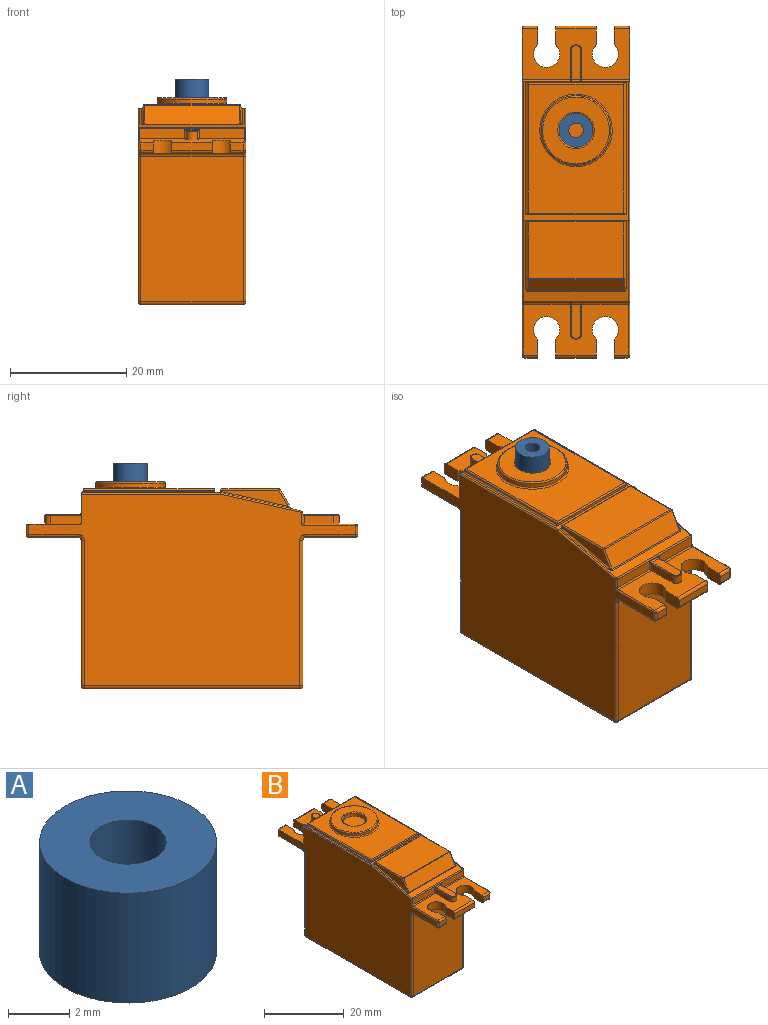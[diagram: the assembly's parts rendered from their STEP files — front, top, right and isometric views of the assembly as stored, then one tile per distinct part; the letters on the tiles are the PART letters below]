
ASSEMBLY  parts=2 mates=1
PART A: 4 faces, bbox 5.8x5.8x4.4 mm
  f0: cylinder r=2.9mm len=5.8mm, axis (0,0,-1), area 80.2mm2, adj f1,f2
  f1: plane 5.8x5.8mm, normal (0,0,1), area 21.5mm2, adj f0,f3
  f2: plane 5.8x5.8mm, normal (0,0,-1), area 21.5mm2, adj f0,f3
  f3: cylinder r=1.25mm len=4.4mm, axis (0,0,1), area 34.6mm2, adj f1,f2
PART B: 154 faces, bbox 18.6x57.2x35.7 mm
  f0: plane 18.1x8.75mm, normal (0,0,1), area 100.9mm2, adj f9,f10,f41,f42,f43,f82,f84,f88
  f1: plane 7x1.3mm, normal (0,-1,0), area 9.1mm2, adj f7,f9,f149,f151
  f2: plane 2.2x1.3mm, normal (0,-1,0), area 2.9mm2, adj f8,f10,f128,f150
  f3: plane 17.6x8.5mm, normal (0,0,-1), area 103.4mm2, adj f13,f14,f106,f108,f109,f140,f142,f143
  f4: plane 7x1.3mm, normal (0,1,0), area 9.1mm2, adj f11,f13,f142,f145
  f5: plane 2.2x1.3mm, normal (0,1,0), area 2.9mm2, adj f12,f14,f139,f144
  f6: plane 18.6x8.75mm, normal (0,0,1), area 105.3mm2, adj f11,f12,f25,f26,f37,f38,f39,f93
  f7: cylinder r=0.5mm len=7mm, axis (-1,0,0), area 5.5mm2, adj f1,f19,f149,f151
  f8: cylinder r=0.5mm len=2.2mm, axis (-1,0,0), area 1.7mm2, adj f2,f19,f129,f150
  f9: cylinder r=0.5mm len=7mm, axis (-1,0,0), area 5.5mm2, adj f0,f1,f149,f151
  f10: cylinder r=0.5mm len=2.45mm, axis (-1,0,0), area 1.8mm2, adj f0,f2,f130,f150
  f11: cylinder r=0.5mm len=7mm, axis (-1,0,0), area 5.5mm2, adj f4,f6,f142,f145
  f12: cylinder r=0.5mm len=2.7mm, axis (-1,0,0), area 1.9mm2, adj f5,f6,f139,f144
  f13: cylinder r=0.5mm len=7mm, axis (-1,0,0), area 5.5mm2, adj f3,f4,f142,f145
  f14: cylinder r=0.5mm len=2.2mm, axis (-1,0,0), area 1.7mm2, adj f3,f5,f141,f144
  f15: plane 18.1x1.75mm, normal (0,-1,0), area 27.8mm2, adj f63,f81,f84,f85,f86,f87,f88,f91
  f16: plane 18.1x14.01mm, normal (0,-0.22,0.98), area 41.1mm2, adj f17,f55,f56,f57,f62,f63,f64,f67
  f17: plane 24x18.1mm, normal (0,0,1), area 36.7mm2, adj f16,f24,f29,f32,f61,f65,f67,f68
  f18: plane 2.2x1.3mm, normal (0,-1,0), area 2.9mm2, adj f131,f132,f135,f152
  f19: plane 17.6x8.5mm, normal (0,0,-1), area 103.4mm2, adj f7,f8,f121,f125,f127,f131,f148,f149
  f20: plane 25.1x17.6mm, normal (0,-1,0), area 441.8mm2, adj f119,f120,f124,f125
  f21: plane 37.2x17.6mm, normal (0,0,-1), area 654.7mm2, adj f114,f115,f118,f119
  f22: plane 25.1x17.6mm, normal (0,1,0), area 441.8mm2, adj f109,f110,f113,f114
  f23: plane 2.2x1.3mm, normal (0,1,0), area 2.9mm2, adj f136,f137,f140,f146
  f24: plane 18.64x5.19mm, normal (0,1,0), area 92.7mm2, adj f17,f25,f26,f38,f39,f61,f65,f93
  f25: plane 56.2x33.05mm, normal (1,0,0), area 1243.7mm2, adj f6,f24,f61,f62,f81,f82,f83,f95
  f26: plane 56.2x33.05mm, normal (-1,0,0), area 1243.7mm2, adj f6,f24,f64,f65,f89,f90,f91,f93
  f27: plane 16.85x0.2mm, normal (0,1,0), area 3.4mm2, adj f30,f31,f70,f74
  f28: plane 22.17x16.35mm, normal (0,0,1), area 239.8mm2, adj f58,f71,f72,f73,f74
  f29: plane 17.35x0.45mm, normal (0,-1,0), area 7.6mm2, adj f17,f30,f31,f68,f69,f71
  f30: plane 22.67x0.2mm, normal (1,0,0), area 4.5mm2, adj f27,f29,f68,f72
  f31: plane 22.67x0.2mm, normal (-1,0,0), area 4.5mm2, adj f27,f29,f69,f73
  f32: plane 17.35x0.47mm, normal (0,1,0), area 7.6mm2, adj f17,f35,f36,f50,f55,f75
  f33: plane 16.35x9.81mm, normal (0,0,1), area 160.3mm2, adj f49,f50,f51,f52
  f34: plane 16.35x3.23mm, normal (0,-0.87,0.5), area 61.1mm2, adj f51,f54,f57,f78
  f35: plane 11.7x2.83mm, normal (1,0,0), area 15.4mm2, adj f32,f52,f54,f55
  f36: plane 11.7x2.83mm, normal (-1,0,0), area 15.4mm2, adj f32,f49,f75,f76,f78
  f37: cylinder r=0.97mm len=1.95mm, axis (0,0,-1), area 4.5mm2, adj f6,f38,f39,f98
  f38: plane 5.28x1.57mm, normal (-1,0,0), area 7.8mm2, adj f6,f24,f37,f93,f96,f97
  f39: plane 5.28x1.57mm, normal (1,0,0), area 7.8mm2, adj f6,f24,f37,f95,f99,f100
  f40: plane 5.88x1.7mm, normal (0,0,1), area 9.7mm2, adj f94,f97,f98,f99
  f41: plane 5.03x1.48mm, normal (-1,0,0), area 7.4mm2, adj f0,f42,f87,f102
  f42: cylinder r=0.97mm len=1.95mm, axis (0,0,-1), area 4.5mm2, adj f0,f41,f43,f103
  f43: plane 5.03x1.48mm, normal (1,0,0), area 7.4mm2, adj f0,f42,f85,f104
  f44: plane 5.88x1.7mm, normal (0,0,1), area 9.7mm2, adj f86,f102,f103,f104
  f45: cylinder r=2.9mm len=5.8mm, axis (0,0,-1), area 17.3mm2, adj f48,f59
  f46: cylinder r=6mm len=12mm, axis (0,0,-1), area 26.4mm2, adj f58,f60
  f47: plane 11.5x11.5mm, normal (0,0,1), area 72.7mm2, adj f59,f60
  f48: plane 5.8x5.8mm, normal (0,0,1), area 26.4mm2, adj f45
  f49: cylinder r=0.25mm len=10.06mm, axis (0,-1,0), area 3.9mm2, adj f33,f36,f50,f79
  f50: cylinder r=0.25mm len=16.85mm, axis (-1,0,0), area 6.5mm2, adj f32,f33,f49,f52
  f51: cylinder r=0.25mm len=16.35mm, axis (1,0,0), area 4.3mm2, adj f33,f34,f53,f79
  f52: cylinder r=0.25mm len=10.06mm, axis (0,1,0), area 3.9mm2, adj f33,f35,f50,f53
  f53: sphere r=0.25mm, area 0.1mm2, adj f51,f52,f54
  f54: cylinder r=0.25mm len=3.36mm, axis (0,0.5,0.87), area 1.4mm2, adj f34,f35,f53,f56
  f55: cylinder r=0.25mm len=11.75mm, axis (0,-0.98,-0.22), area 4.7mm2, adj f16,f32,f35,f56
  f56: bspline ~0.78x0.52mm, area 0.2mm2, adj f16,f54,f55,f57
  f57: cylinder r=0.25mm len=16.35mm, axis (-1,0,0), area 3.4mm2, adj f16,f34,f56,f77
  f58: torus R=6.25mm, axis (0,0,-1), area 15mm2, adj f28,f46
  f59: torus R=3.15mm, axis (0,0,1), area 7.4mm2, adj f45,f47
  f60: torus R=5.75mm, axis (0,0,1), area 14.6mm2, adj f46,f47
  f61: cylinder r=0.25mm len=24mm, axis (0,1,0), area 9.4mm2, adj f17,f24,f25,f62
  f62: cylinder r=0.25mm len=14.06mm, axis (0,0.98,0.22), area 5.6mm2, adj f16,f25,f61,f80
  f63: cylinder r=0.25mm len=18.1mm, axis (-1,0,0), area 6.1mm2, adj f15,f16,f80,f92
  f64: cylinder r=0.25mm len=14.03mm, axis (0,-0.98,-0.22), area 5.6mm2, adj f16,f26,f66,f92
  f65: cylinder r=0.25mm len=23.97mm, axis (0,-1,0), area 9.4mm2, adj f17,f24,f26,f66
  f66: sphere r=0.25mm, area 0mm2, adj f64,f65,f67
  f67: cylinder r=0.25mm len=0.38mm, axis (-1,0,0), area 0mm2, adj f16,f17,f66,f75
  f68: cylinder r=0.25mm len=22.92mm, axis (0,-1,0), area 9mm2, adj f17,f29,f30,f70
  f69: cylinder r=0.25mm len=22.92mm, axis (0,1,0), area 9mm2, adj f17,f29,f31,f70
  f70: cylinder r=0.25mm len=17.35mm, axis (-1,0,0), area 6.7mm2, adj f17,f27,f68,f69
  f71: cylinder r=0.25mm len=16.85mm, axis (1,0,0), area 6.5mm2, adj f28,f29,f72,f73
  f72: cylinder r=0.25mm len=22.67mm, axis (0,1,0), area 8.8mm2, adj f28,f30,f71,f74
  f73: cylinder r=0.25mm len=22.67mm, axis (0,-1,0), area 8.8mm2, adj f28,f31,f71,f74
  f74: cylinder r=0.25mm len=16.85mm, axis (1,0,0), area 6.5mm2, adj f27,f28,f72,f73
  f75: torus R=0.5mm, axis (1,0,0), area 0mm2, adj f17,f32,f36,f67,f76
  f76: cylinder r=0.25mm len=11.67mm, axis (0,0.98,0.22), area 4.7mm2, adj f16,f36,f75,f77
  f77: bspline ~0.78x0.5mm, area 0.2mm2, adj f16,f57,f76,f78
  f78: cylinder r=0.25mm len=3.36mm, axis (0,-0.5,-0.87), area 1.4mm2, adj f34,f36,f77,f79
  f79: sphere r=0.25mm, area 0.1mm2, adj f49,f51,f78
  f80: sphere r=0.25mm, area 0.1mm2, adj f62,f63,f81
  f81: cylinder r=0.25mm len=1.75mm, axis (0,0,1), area 0.7mm2, adj f15,f25,f80,f83
  f82: cylinder r=0.25mm len=8.75mm, axis (0,1,0), area 3.4mm2, adj f0,f25,f83,f134
  f83: torus R=0.5mm, axis (1,0,0), area 0.2mm2, adj f25,f81,f82,f84
  f84: cylinder r=0.25mm len=8.08mm, axis (-1,0,0), area 3.1mm2, adj f0,f15,f83,f85
  f85: cylinder r=0.25mm len=1.85mm, axis (0,0,-1), area 0.6mm2, adj f15,f43,f84,f105
  f86: cylinder r=0.25mm len=2.45mm, axis (1,0,0), area 0.8mm2, adj f15,f44,f101,f105
  f87: cylinder r=0.25mm len=1.85mm, axis (0,0,-1), area 0.6mm2, adj f15,f41,f88,f101
  f88: cylinder r=0.25mm len=8.08mm, axis (-1,0,0), area 3.1mm2, adj f0,f15,f87,f90
  f89: cylinder r=0.25mm len=8.75mm, axis (0,-1,0), area 3.4mm2, adj f0,f26,f90,f130
  f90: torus R=0.5mm, axis (1,0,0), area 0.2mm2, adj f26,f88,f89,f91
  f91: cylinder r=0.25mm len=1.75mm, axis (0,0,-1), area 0.7mm2, adj f15,f26,f90,f92
  f92: sphere r=0.25mm, area 0.1mm2, adj f63,f64,f91
  f93: cylinder r=0.25mm len=8.33mm, axis (-1,0,0), area 3.3mm2, adj f6,f24,f26,f38
  f94: cylinder r=0.25mm len=1.7mm, axis (1,0,0), area 0.7mm2, adj f24,f40,f96,f100
  f95: cylinder r=0.25mm len=8.33mm, axis (-1,0,0), area 3.3mm2, adj f6,f24,f25,f39
  f96: torus R=0.38mm, axis (1,0,0), area 0.1mm2, adj f24,f38,f94,f97
  f97: cylinder r=0.12mm len=5.03mm, axis (0,1,0), area 1mm2, adj f38,f40,f96,f98
  f98: torus R=0.85mm, axis (0,0,1), area 0.6mm2, adj f37,f40,f97,f99
  f99: cylinder r=0.12mm len=5.03mm, axis (0,-1,0), area 1mm2, adj f39,f40,f98,f100
  f100: torus R=0.38mm, axis (-1,0,0), area 0.1mm2, adj f24,f39,f94,f99
  f101: bspline ~0.38x0.38mm, area 0mm2, adj f86,f87,f102
  f102: cylinder r=0.12mm len=5.03mm, axis (0,1,0), area 1mm2, adj f41,f44,f101,f103
  f103: torus R=0.85mm, axis (0,0,1), area 0.6mm2, adj f42,f44,f102,f104
  f104: cylinder r=0.12mm len=5.03mm, axis (0,-1,0), area 1mm2, adj f43,f44,f103,f105
  f105: bspline ~0.38x0.38mm, area 0mm2, adj f85,f86,f104
  f106: cylinder r=0.5mm len=8.5mm, axis (0,1,0), area 6.7mm2, adj f3,f26,f107,f138
  f107: torus R=1mm, axis (1,0,0), area 0.8mm2, adj f26,f106,f109,f110
  f108: cylinder r=0.5mm len=8.5mm, axis (0,-1,0), area 6.7mm2, adj f3,f25,f111,f141
  f109: cylinder r=0.5mm len=17.6mm, axis (-1,0,0), area 13.8mm2, adj f3,f22,f107,f111
  f110: cylinder r=0.5mm len=25.1mm, axis (0,0,1), area 19.7mm2, adj f22,f26,f107,f112
  f111: torus R=1mm, axis (1,0,0), area 0.8mm2, adj f25,f108,f109,f113
  f112: sphere r=0.5mm, area 0.4mm2, adj f110,f114,f115
  f113: cylinder r=0.5mm len=25.1mm, axis (0,0,-1), area 19.7mm2, adj f22,f25,f111,f116
  f114: cylinder r=0.5mm len=17.6mm, axis (-1,0,0), area 13.8mm2, adj f21,f22,f112,f116
  f115: cylinder r=0.5mm len=37.2mm, axis (0,1,0), area 29.2mm2, adj f21,f26,f112,f117
  f116: sphere r=0.5mm, area 0.4mm2, adj f113,f114,f118
  f117: sphere r=0.5mm, area 0.4mm2, adj f115,f119,f120
  f118: cylinder r=0.5mm len=37.2mm, axis (0,-1,0), area 29.2mm2, adj f21,f25,f116,f122
  f119: cylinder r=0.5mm len=17.6mm, axis (1,0,0), area 13.8mm2, adj f20,f21,f117,f122
  f120: cylinder r=0.5mm len=25.1mm, axis (0,0,-1), area 19.7mm2, adj f20,f26,f117,f123
  f121: cylinder r=0.5mm len=8.5mm, axis (0,1,0), area 6.7mm2, adj f19,f26,f123,f129
  f122: sphere r=0.5mm, area 0.4mm2, adj f118,f119,f124
  f123: torus R=1mm, axis (1,0,0), area 0.8mm2, adj f26,f120,f121,f125
  f124: cylinder r=0.5mm len=25.1mm, axis (0,0,1), area 19.7mm2, adj f20,f25,f122,f126
  f125: cylinder r=0.5mm len=17.6mm, axis (-1,0,0), area 13.8mm2, adj f19,f20,f123,f126
  f126: torus R=1mm, axis (1,0,0), area 0.8mm2, adj f25,f124,f125,f127
  f127: cylinder r=0.5mm len=8.5mm, axis (0,-1,0), area 6.7mm2, adj f19,f25,f126,f133
  f128: cylinder r=0.5mm len=1.55mm, axis (0,0,-1), area 1.1mm2, adj f2,f26,f129,f130
  f129: sphere r=0.5mm, area 0.4mm2, adj f8,f121,f128
  f130: bspline ~0.52x0.5mm, area 0.1mm2, adj f10,f89,f128
  f131: cylinder r=0.5mm len=2.2mm, axis (-1,0,0), area 1.7mm2, adj f18,f19,f133,f152
  f132: cylinder r=0.5mm len=2.45mm, axis (-1,0,0), area 1.8mm2, adj f0,f18,f134,f152
  f133: sphere r=0.5mm, area 0.4mm2, adj f127,f131,f135
  f134: bspline ~0.52x0.5mm, area 0.1mm2, adj f82,f132,f135
  f135: cylinder r=0.5mm len=1.55mm, axis (0,0,1), area 1.1mm2, adj f18,f25,f133,f134
  f136: cylinder r=0.5mm len=1.8mm, axis (0,0,1), area 1.2mm2, adj f23,f26,f137,f138
  f137: cylinder r=0.5mm len=2.7mm, axis (-1,0,0), area 1.9mm2, adj f6,f23,f136,f146
  f138: sphere r=0.5mm, area 0.4mm2, adj f106,f136,f140
  f139: cylinder r=0.5mm len=1.8mm, axis (0,0,-1), area 1.2mm2, adj f5,f12,f25,f141
  f140: cylinder r=0.5mm len=2.2mm, axis (-1,0,0), area 1.7mm2, adj f3,f23,f138,f146
  f141: sphere r=0.5mm, area 0.4mm2, adj f14,f108,f139
  f142: plane 3.24x2.3mm, normal (1,0,0), area 7.4mm2, adj f3,f4,f6,f11,f13,f143
  f143: cylinder r=2.25mm len=4.5mm, axis (0,0,1), area 24.6mm2, adj f3,f6,f142,f144
  f144: plane 3.24x2.3mm, normal (-1,0,0), area 7.4mm2, adj f3,f5,f6,f12,f14,f143
  f145: plane 3.24x2.3mm, normal (-1,0,0), area 7.4mm2, adj f3,f4,f6,f11,f13,f147
  f146: plane 3.24x2.3mm, normal (1,0,0), area 7.4mm2, adj f3,f6,f23,f137,f140,f147
  f147: cylinder r=2.25mm len=4.5mm, axis (0,0,1), area 24.6mm2, adj f3,f6,f145,f146
  f148: cylinder r=2.25mm len=4.5mm, axis (0,0,1), area 24.6mm2, adj f0,f19,f149,f150
  f149: plane 3.24x2.3mm, normal (-1,0,0), area 7.4mm2, adj f0,f1,f7,f9,f19,f148
  f150: plane 3.24x2.3mm, normal (1,0,0), area 7.4mm2, adj f0,f2,f8,f10,f19,f148
  f151: plane 3.24x2.3mm, normal (1,0,0), area 7.4mm2, adj f0,f1,f7,f9,f19,f153
  f152: plane 3.24x2.3mm, normal (-1,0,0), area 7.4mm2, adj f0,f18,f19,f131,f132,f153
  f153: cylinder r=2.25mm len=4.5mm, axis (0,0,1), area 24.6mm2, adj f0,f19,f151,f152
PLACE A at identity
PLACE B at identity fixed
MATE revolute A.f0 <-> B.f45  axis (0,0,-1) through (0,10.6,17.25)mm
